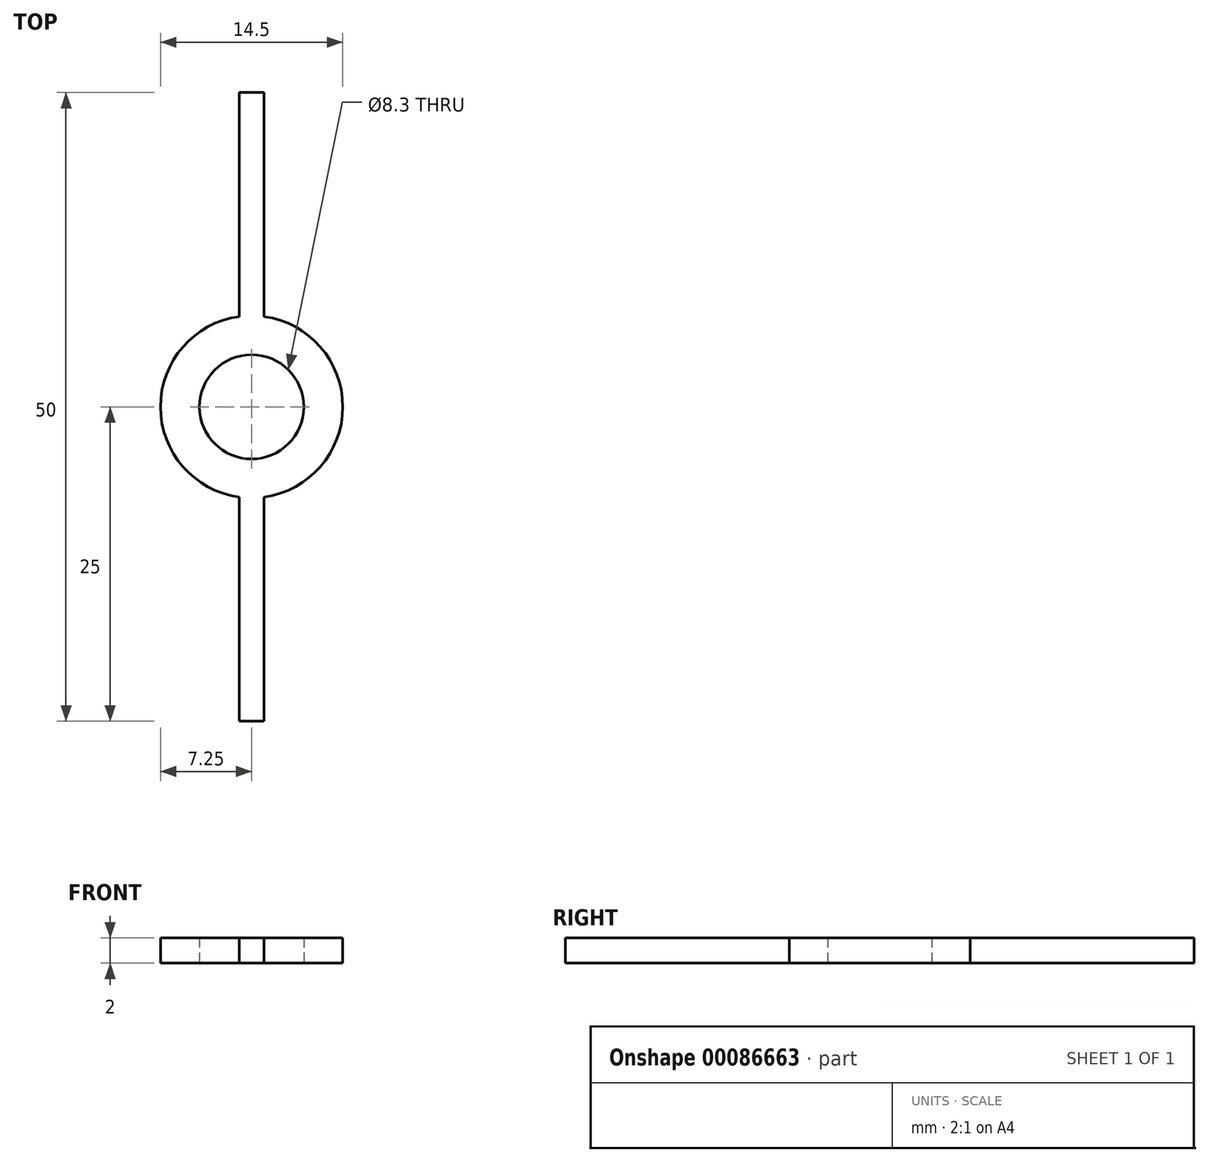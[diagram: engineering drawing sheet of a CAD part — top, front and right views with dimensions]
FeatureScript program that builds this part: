
annotation { "Feature Type Name" : "Feature", "Feature Type Description" : "" }
export const myFeature = defineFeature(function(context is Context, id is Id, definition is map)
    precondition{}
    {
        {
            var Q0;
            Q0=qCreatedBy(makeId("Top.planeOp"),FACE);
            var sketch = newSketch(context, id + "F0", { "sketchPlane" : qUnion([Q0])});
            skCircle(sketch, "E0", {"center": v(0, 0) * mm, "radius": 7.25 * mm});
            skSolve(sketch);
        }
        {
            var Q0;
            Q0=makeQuery(id+"F0.imprint","IMPRINT",FACE,{"disambiguationData":[TD([[makeQuery(id+"F0.imprint","IMPRINT",EDGE,{"derivedFrom":sQuery(id+"F0.wireOp",EDGE,"E0")}),1.0]])]});
            extrude(context, id + "F1", {"entities" : qUnion([Q0]), "depth" : 2 * mm});
        }
        {
            var Q0;
            Q0=qCreatedBy(makeId("Front.planeOp"),FACE);
            var sketch = newSketch(context, id + "F4", { "sketchPlane" : qUnion([Q0])});
            skLineSegment(sketch, "E1.bottom", {"start": v(1, 2) * mm, "end": v(-1, 2) * mm});
            skLineSegment(sketch, "E1.top", {"start": v(1, 0) * mm, "end": v(-1, 0) * mm});
            skLineSegment(sketch, "E1.left", {"start": v(1, 2) * mm, "end": v(1, 0) * mm});
            skLineSegment(sketch, "E1.right", {"start": v(-1, 2) * mm, "end": v(-1, 0) * mm});
            skPoint(sketch, "E1.middle", {"position": v(0, 1) * mm});
            skSolve(sketch);
        }
        {
            var Q0;
            Q0 = qSketchRegion(id + "F4", true);
            extrude(context, id + "F2", {"entities" : qUnion([Q0]), "operationType" : NewBodyOperationType.ADD, "depth" : 25 * mm, "hasSecondDirection" : true, "secondDirectionOppositeDirection" : true, "secondDirectionDepth" : 25 * mm});
        }
        {
            var Q0;
            Q0=makeQuery(id+"F2.boolean.opBoolean","MERGE",FACE,{"derivedFrom":[makeQuery(id+"F1.opExtrude","CAP_FACE",FACE,{"disambiguationData":[OSD([sQuery(id+"F0.wireOp",EDGE,"E0")])],"isStart":true}),makeQuery(id+"F2.opExtrude","SWEPT_FACE",FACE,{"disambiguationData":[OSD([sQuery(id+"F4.wireOp",EDGE,"E1.top")])]})]});
            var sketch = newSketch(context, id + "F3", { "sketchPlane" : qUnion([Q0])});
            skCircle(sketch, "E2", {"center": v(0, 0) * mm, "radius": 4.15 * mm});
            skSolve(sketch);
        }
        {
            var Q0;
            Q0 = qSketchRegion(id + "F3", true);
            extrude(context, id + "F5", {"entities" : qUnion([Q0]), "operationType" : NewBodyOperationType.REMOVE, "oppositeDirection" : true, "depth" : 25 * mm});
        }
    });
